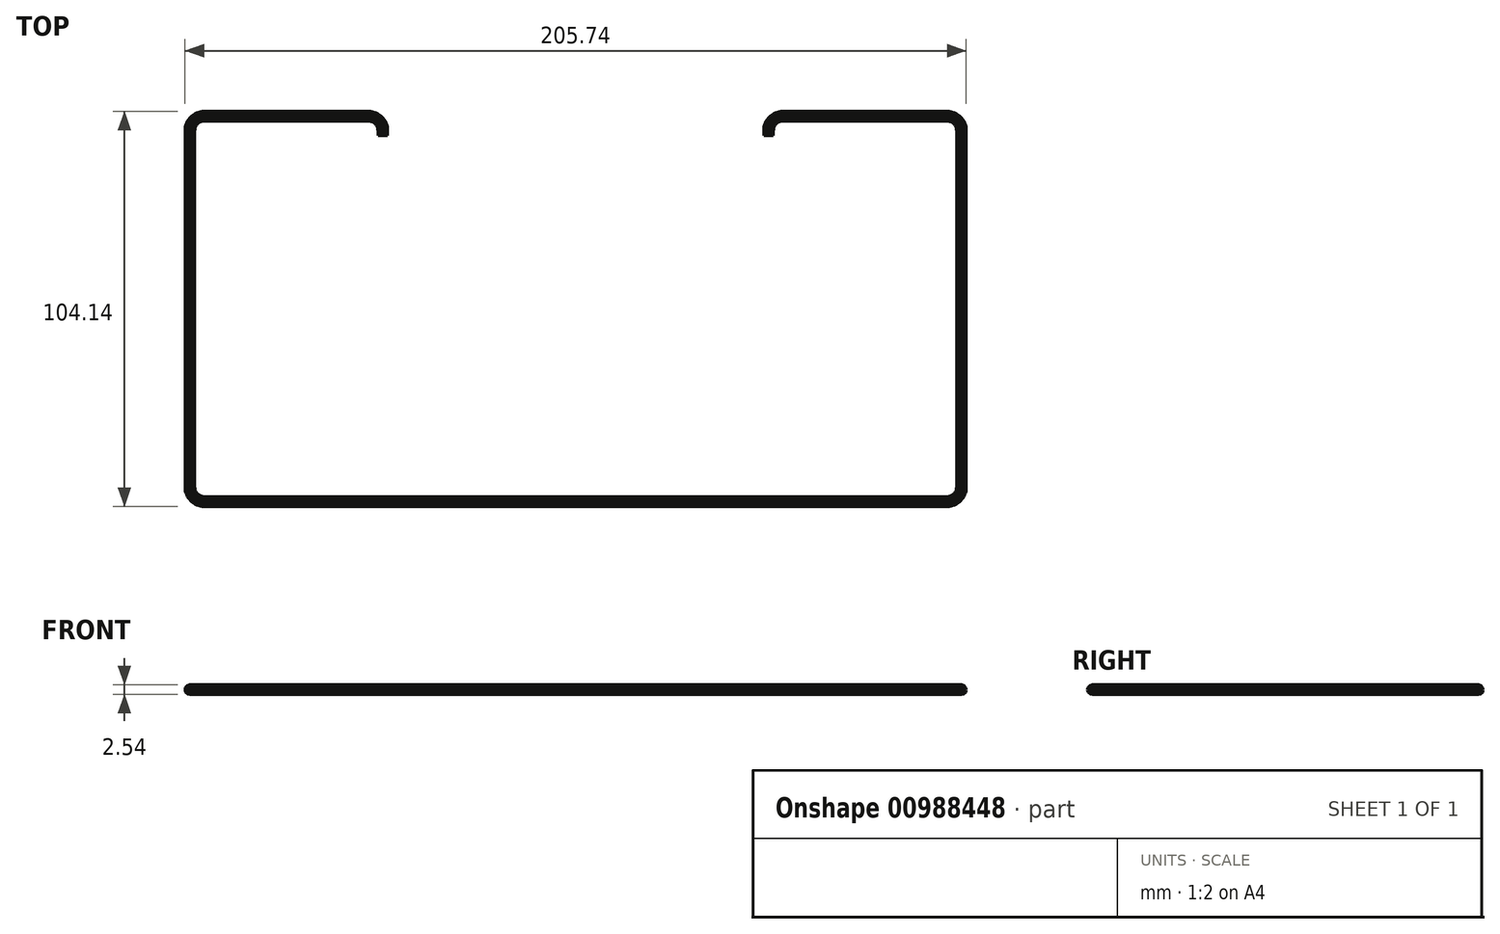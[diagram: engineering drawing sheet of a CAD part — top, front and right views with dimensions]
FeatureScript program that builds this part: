
annotation { "Feature Type Name" : "Feature", "Feature Type Description" : "" }
export const myFeature = defineFeature(function(context is Context, id is Id, definition is map)
    precondition{}
    {
        {
            var Q0;
            Q0=qCreatedBy(makeId("Top.planeOp"),FACE);
            var sketch = newSketch(context, id + "F0", { "sketchPlane" : qUnion([Q0])});
            skLineSegment(sketch, "E0", {"start": v(0, 0) * mm, "end": v(-97.8, 0) * mm});
            skLineSegment(sketch, "E1", {"start": v(-101.6, 3.8) * mm, "end": v(-101.6, 97.8) * mm});
            skLineSegment(sketch, "E2", {"start": v(-97.8, 101.6) * mm, "end": v(-54.61, 101.6) * mm});
            skLineSegment(sketch, "E3", {"start": v(-50.8, 97.8) * mm, "end": v(-50.8, 96.52) * mm});
            skPoint(sketch, "E4.visualSharp", {"position": v(-101.6, 101.6) * mm});
            skArc(sketch, "E4.filletArc", {"start": v(-97.8, 101.6) * mm, "mid": v(-100.48, 100.48) * mm, "end": v(-101.6, 97.8) * mm});
            skPoint(sketch, "E5.visualSharp", {"position": v(-101.6, 0) * mm});
            skArc(sketch, "E5.filletArc", {"start": v(-101.6, 3.8) * mm, "mid": v(-100.48, 1.12) * mm, "end": v(-97.8, 0) * mm});
            skPoint(sketch, "E6.visualSharp", {"position": v(-50.8, 101.6) * mm});
            skArc(sketch, "E6.filletArc", {"start": v(-50.8, 97.8) * mm, "mid": v(-51.92, 100.48) * mm, "end": v(-54.61, 101.6) * mm});
            skSolve(sketch);
        }
        {
            var Q0;
            Q0=qCreatedBy(makeId("Right.planeOp"),FACE);
            var sketch = newSketch(context, id + "F1", { "sketchPlane" : qUnion([Q0])});
            skCircle(sketch, "E7.cCircle", {"center": v(0, 0) * mm, "radius": 1.27 * mm, "construction": true});
            skLineSegment(sketch, "E7.0", {"start": v(1.15, -0.55) * mm, "end": v(0.72, -1.05) * mm});
            skLineSegment(sketch, "E7.1", {"start": v(0.72, -1.05) * mm, "end": v(0.1, -1.27) * mm});
            skLineSegment(sketch, "E7.2", {"start": v(0.1, -1.27) * mm, "end": v(-0.55, -1.15) * mm});
            skLineSegment(sketch, "E7.3", {"start": v(-0.55, -1.15) * mm, "end": v(-1.05, -0.72) * mm});
            skLineSegment(sketch, "E7.4", {"start": v(-1.05, -0.72) * mm, "end": v(-1.27, -0.1) * mm});
            skLineSegment(sketch, "E7.5", {"start": v(-1.27, -0.1) * mm, "end": v(-1.15, 0.55) * mm});
            skLineSegment(sketch, "E7.6", {"start": v(-1.15, 0.55) * mm, "end": v(-0.72, 1.05) * mm});
            skLineSegment(sketch, "E7.7", {"start": v(-0.72, 1.05) * mm, "end": v(-0.1, 1.27) * mm});
            skLineSegment(sketch, "E7.8", {"start": v(-0.1, 1.27) * mm, "end": v(0.55, 1.15) * mm});
            skLineSegment(sketch, "E7.9", {"start": v(0.55, 1.15) * mm, "end": v(1.05, 0.72) * mm});
            skLineSegment(sketch, "E7.10", {"start": v(1.05, 0.72) * mm, "end": v(1.27, 0.1) * mm});
            skLineSegment(sketch, "E7.11", {"start": v(1.27, 0.1) * mm, "end": v(1.15, -0.55) * mm});
            skSolve(sketch);
        }
        {
            var Q0;
            Q0=makeQuery(id+"F1.imprint","IMPRINT",FACE,{"disambiguationData":[TD([[makeQuery(id+"F1.imprint","IMPRINT",EDGE,{"derivedFrom":sQuery(id+"F1.wireOp",EDGE,"E7.0")}),-1.0]])]});
            var Q1;
            Q1=sQuery(id+"F0.wireOp",EDGE,"E0");
            var Q2;
            Q2=sQuery(id+"F0.wireOp",EDGE,"E5.filletArc");
            var Q3;
            Q3=sQuery(id+"F0.wireOp",EDGE,"E1");
            var Q4;
            Q4=sQuery(id+"F0.wireOp",EDGE,"E4.filletArc");
            var Q5;
            Q5=sQuery(id+"F0.wireOp",EDGE,"E2");
            var Q6;
            Q6=sQuery(id+"F0.wireOp",EDGE,"E6.filletArc");
            var Q7;
            Q7=sQuery(id+"F0.wireOp",EDGE,"E3");
            sweep(context, id + "F2", {"profiles" : qUnion([Q0]), "path" : qUnion([Q1, Q2, Q3, Q4, Q5, Q6, Q7])});
        }
        {
            var Q0;
            Q0=makeQuery(id+"F2.opSweep","SWEPT_BODY",BODY,{"disambiguationData":[OSD([sQuery(id+"F0.wireOp",EDGE,"E3"),sQuery(id+"F1.wireOp",EDGE,"E7.0"),sQuery(id+"F1.wireOp",EDGE,"E7.1"),sQuery(id+"F1.wireOp",EDGE,"E7.2"),sQuery(id+"F1.wireOp",EDGE,"E7.3"),sQuery(id+"F1.wireOp",EDGE,"E7.4"),sQuery(id+"F1.wireOp",EDGE,"E7.5"),sQuery(id+"F1.wireOp",EDGE,"E7.6"),sQuery(id+"F1.wireOp",EDGE,"E7.7"),sQuery(id+"F1.wireOp",EDGE,"E7.8"),sQuery(id+"F1.wireOp",EDGE,"E7.9"),sQuery(id+"F1.wireOp",EDGE,"E7.10"),sQuery(id+"F1.wireOp",EDGE,"E7.11")])]});
            var Q1;
            Q1=qCreatedBy(makeId("Right.planeOp"),FACE);
            mirror(context, id + "F3", {"operationType" : NewBodyOperationType.ADD, "entities" : qUnion([Q0]), "mirrorPlane" : qUnion([Q1])});
        }
    });
